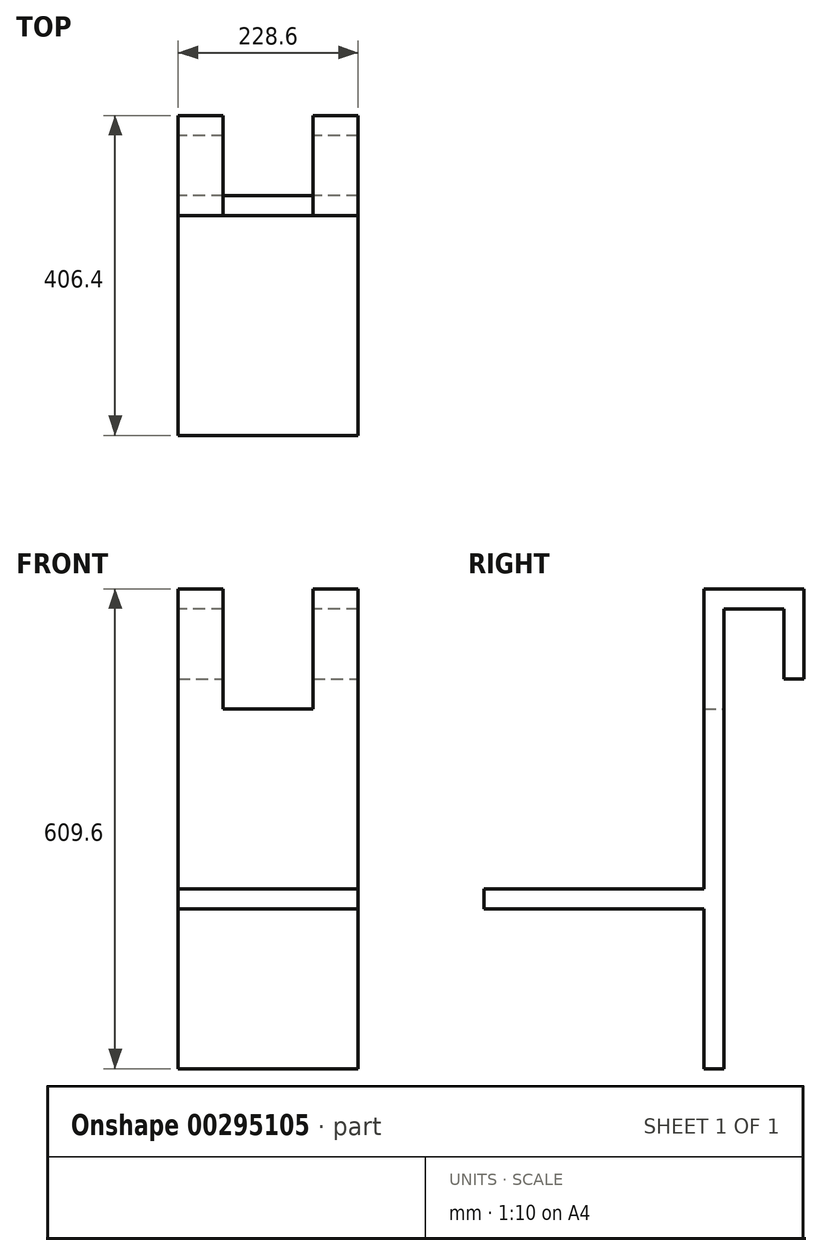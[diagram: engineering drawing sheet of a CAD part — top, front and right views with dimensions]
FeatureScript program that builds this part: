
annotation { "Feature Type Name" : "Feature", "Feature Type Description" : "" }
export const myFeature = defineFeature(function(context is Context, id is Id, definition is map)
    precondition{}
    {
        {
            var Q0;
            Q0=qCreatedBy(makeId("Front.planeOp"),FACE);
            var sketch = newSketch(context, id + "F0", { "sketchPlane" : qUnion([Q0])});
            skLineSegment(sketch, "E0.bottom", {"start": v(-228.64, 291.42) * mm, "end": v(-171.5, 291.42) * mm});
            skLineSegment(sketch, "E0.top", {"start": v(-228.64, -318.18) * mm, "end": v(-0.04, -318.18) * mm});
            skLineSegment(sketch, "E0.left", {"start": v(-228.64, 291.42) * mm, "end": v(-228.64, -318.18) * mm});
            skLineSegment(sketch, "E0.right", {"start": v(-0.04, 291.42) * mm, "end": v(-0.04, -318.18) * mm});
            skPoint(sketch, "E1", {"position": v(-114.34, 291.42) * mm});
            skPoint(sketch, "E2", {"position": v(-57.2, 291.42) * mm});
            skPoint(sketch, "E3", {"position": v(-171.5, 291.42) * mm});
            skLineSegment(sketch, "E4.top", {"start": v(-171.5, 139.02) * mm, "end": v(-57.2, 139.02) * mm});
            skLineSegment(sketch, "E4.left", {"start": v(-171.5, 291.42) * mm, "end": v(-171.5, 139.02) * mm});
            skLineSegment(sketch, "E4.right", {"start": v(-57.2, 291.42) * mm, "end": v(-57.2, 139.02) * mm});
            skLineSegment(sketch, "E5.trimOffspring", {"start": v(-57.2, 291.42) * mm, "end": v(-0.04, 291.42) * mm});
            skSolve(sketch);
        }
        {
            var Q0;
            Q0=makeQuery(id+"F0.imprint","IMPRINT",FACE,{"disambiguationData":[TD([[makeQuery(id+"F0.imprint","IMPRINT",EDGE,{"derivedFrom":sQuery(id+"F0.wireOp",EDGE,"E0.bottom")}),-1.0]])]});
            extrude(context, id + "F1", {"entities" : qUnion([Q0]), "depth" : 25.4 * mm});
        }
        {
            var Q0;
            Q0=makeQuery(id+"F1.opExtrude","CAP_FACE",FACE,{"disambiguationData":[OSD([sQuery(id+"F0.wireOp",EDGE,"E0.bottom"),sQuery(id+"F0.wireOp",EDGE,"E0.top"),sQuery(id+"F0.wireOp",EDGE,"E0.left"),sQuery(id+"F0.wireOp",EDGE,"E0.right"),sQuery(id+"F0.wireOp",EDGE,"E4.top"),sQuery(id+"F0.wireOp",EDGE,"E4.left"),sQuery(id+"F0.wireOp",EDGE,"E4.right"),sQuery(id+"F0.wireOp",EDGE,"E5.trimOffspring")])],"isStart":true});
            var sketch = newSketch(context, id + "F2", { "sketchPlane" : qUnion([Q0])});
            skLineSegment(sketch, "E6.bottom", {"start": v(0.04, 291.42) * mm, "end": v(57.2, 291.42) * mm});
            skLineSegment(sketch, "E6.top", {"start": v(0.04, 266.02) * mm, "end": v(57.2, 266.02) * mm});
            skLineSegment(sketch, "E6.left", {"start": v(0.04, 291.42) * mm, "end": v(0.04, 266.02) * mm});
            skLineSegment(sketch, "E6.right", {"start": v(57.2, 291.42) * mm, "end": v(57.2, 266.02) * mm});
            skLineSegment(sketch, "E7.bottom", {"start": v(171.5, 291.42) * mm, "end": v(228.64, 291.42) * mm});
            skLineSegment(sketch, "E7.top", {"start": v(171.5, 266.02) * mm, "end": v(228.64, 266.02) * mm});
            skLineSegment(sketch, "E7.left", {"start": v(171.5, 291.42) * mm, "end": v(171.5, 266.02) * mm});
            skLineSegment(sketch, "E7.right", {"start": v(228.64, 291.42) * mm, "end": v(228.64, 266.02) * mm});
            skSolve(sketch);
        }
        {
            var Q0;
            Q0=makeQuery(id+"F2.imprint","IMPRINT",FACE,{"disambiguationData":[TD([[makeQuery(id+"F2.imprint","IMPRINT",EDGE,{"derivedFrom":sQuery(id+"F2.wireOp",EDGE,"E6.bottom")}),1.0]])]});
            var Q1;
            Q1=makeQuery(id+"F2.imprint","IMPRINT",FACE,{"disambiguationData":[TD([[makeQuery(id+"F2.imprint","IMPRINT",EDGE,{"derivedFrom":sQuery(id+"F2.wireOp",EDGE,"E7.bottom")}),1.0]])]});
            extrude(context, id + "F3", {"entities" : qUnion([Q0, Q1]), "operationType" : NewBodyOperationType.ADD, "depth" : 76.2 * mm});
        }
        {
            var Q0;
            Q0=makeQuery(id+"F3.boolean.opBoolean","MERGE",FACE,{"derivedFrom":[makeQuery(id+"F1.opExtrude","SWEPT_FACE",FACE,{"disambiguationData":[OSD([sQuery(id+"F0.wireOp",EDGE,"E5.trimOffspring")])]}),makeQuery(id+"F3.opExtrude","SWEPT_FACE",FACE,{"disambiguationData":[OSD([sQuery(id+"F2.wireOp",EDGE,"E6.bottom")])]})]});
            var sketch = newSketch(context, id + "F4", { "sketchPlane" : qUnion([Q0])});
            skLineSegment(sketch, "E8.bottom", {"start": v(-0.04, 76.2) * mm, "end": v(-57.2, 76.2) * mm});
            skLineSegment(sketch, "E8.top", {"start": v(-0.04, 101.6) * mm, "end": v(-57.2, 101.6) * mm});
            skLineSegment(sketch, "E8.left", {"start": v(-0.04, 76.2) * mm, "end": v(-0.04, 101.6) * mm});
            skLineSegment(sketch, "E8.right", {"start": v(-57.2, 76.2) * mm, "end": v(-57.2, 101.6) * mm});
            skSolve(sketch);
        }
        {
            var Q0;
            Q0=makeQuery(id+"F4.imprint","IMPRINT",FACE,{"disambiguationData":[TD([[makeQuery(id+"F4.imprint","IMPRINT",EDGE,{"derivedFrom":sQuery(id+"F4.wireOp",EDGE,"E8.bottom")}),1.0]])]});
            extrude(context, id + "F5", {"entities" : qUnion([Q0]), "operationType" : NewBodyOperationType.ADD, "oppositeDirection" : true, "depth" : 114.3 * mm});
        }
        {
            var Q0;
            Q0=makeQuery(id+"F3.boolean.opBoolean","MERGE",FACE,{"derivedFrom":[makeQuery(id+"F1.opExtrude","SWEPT_FACE",FACE,{"disambiguationData":[OSD([sQuery(id+"F0.wireOp",EDGE,"E0.bottom")])]}),makeQuery(id+"F3.opExtrude","SWEPT_FACE",FACE,{"disambiguationData":[OSD([sQuery(id+"F2.wireOp",EDGE,"E7.bottom")])]})]});
            var sketch = newSketch(context, id + "F6", { "sketchPlane" : qUnion([Q0])});
            skLineSegment(sketch, "E9.bottom", {"start": v(-171.5, 76.2) * mm, "end": v(-228.64, 76.2) * mm});
            skLineSegment(sketch, "E9.top", {"start": v(-171.5, 101.6) * mm, "end": v(-228.64, 101.6) * mm});
            skLineSegment(sketch, "E9.left", {"start": v(-171.5, 76.2) * mm, "end": v(-171.5, 101.6) * mm});
            skLineSegment(sketch, "E9.right", {"start": v(-228.64, 76.2) * mm, "end": v(-228.64, 101.6) * mm});
            skSolve(sketch);
        }
        {
            var Q0;
            Q0=makeQuery(id+"F6.imprint","IMPRINT",FACE,{"disambiguationData":[TD([[makeQuery(id+"F6.imprint","IMPRINT",EDGE,{"derivedFrom":sQuery(id+"F6.wireOp",EDGE,"E9.bottom")}),1.0]])]});
            extrude(context, id + "F7", {"entities" : qUnion([Q0]), "operationType" : NewBodyOperationType.ADD, "oppositeDirection" : true, "depth" : 114.3 * mm});
        }
        {
            var Q0;
            Q0=makeQuery(id+"F1.opExtrude","CAP_FACE",FACE,{"disambiguationData":[OSD([sQuery(id+"F0.wireOp",EDGE,"E0.bottom"),sQuery(id+"F0.wireOp",EDGE,"E0.top"),sQuery(id+"F0.wireOp",EDGE,"E0.left"),sQuery(id+"F0.wireOp",EDGE,"E0.right"),sQuery(id+"F0.wireOp",EDGE,"E4.top"),sQuery(id+"F0.wireOp",EDGE,"E4.left"),sQuery(id+"F0.wireOp",EDGE,"E4.right"),sQuery(id+"F0.wireOp",EDGE,"E5.trimOffspring")])],"isStart":false});
            var sketch = newSketch(context, id + "F8", { "sketchPlane" : qUnion([Q0])});
            skPoint(sketch, "E10", {"position": v(-228.64, -114.98) * mm});
            skPoint(sketch, "E11", {"position": v(-0.04, -114.98) * mm});
            skLineSegment(sketch, "E12.bottom", {"start": v(-228.64, -114.98) * mm, "end": v(-0.04, -114.98) * mm});
            skLineSegment(sketch, "E12.top", {"start": v(-228.64, -89.58) * mm, "end": v(-0.04, -89.58) * mm});
            skLineSegment(sketch, "E12.left", {"start": v(-228.64, -114.98) * mm, "end": v(-228.64, -89.58) * mm});
            skLineSegment(sketch, "E12.right", {"start": v(-0.04, -114.98) * mm, "end": v(-0.04, -89.58) * mm});
            skSolve(sketch);
        }
        {
            var Q0;
            Q0=makeQuery(id+"F8.imprint","IMPRINT",FACE,{"disambiguationData":[TD([[makeQuery(id+"F8.imprint","IMPRINT",EDGE,{"derivedFrom":sQuery(id+"F8.wireOp",EDGE,"E12.bottom")}),1.0]])]});
            extrude(context, id + "F9", {"entities" : qUnion([Q0]), "operationType" : NewBodyOperationType.ADD, "depth" : 279.4 * mm});
        }
    });
